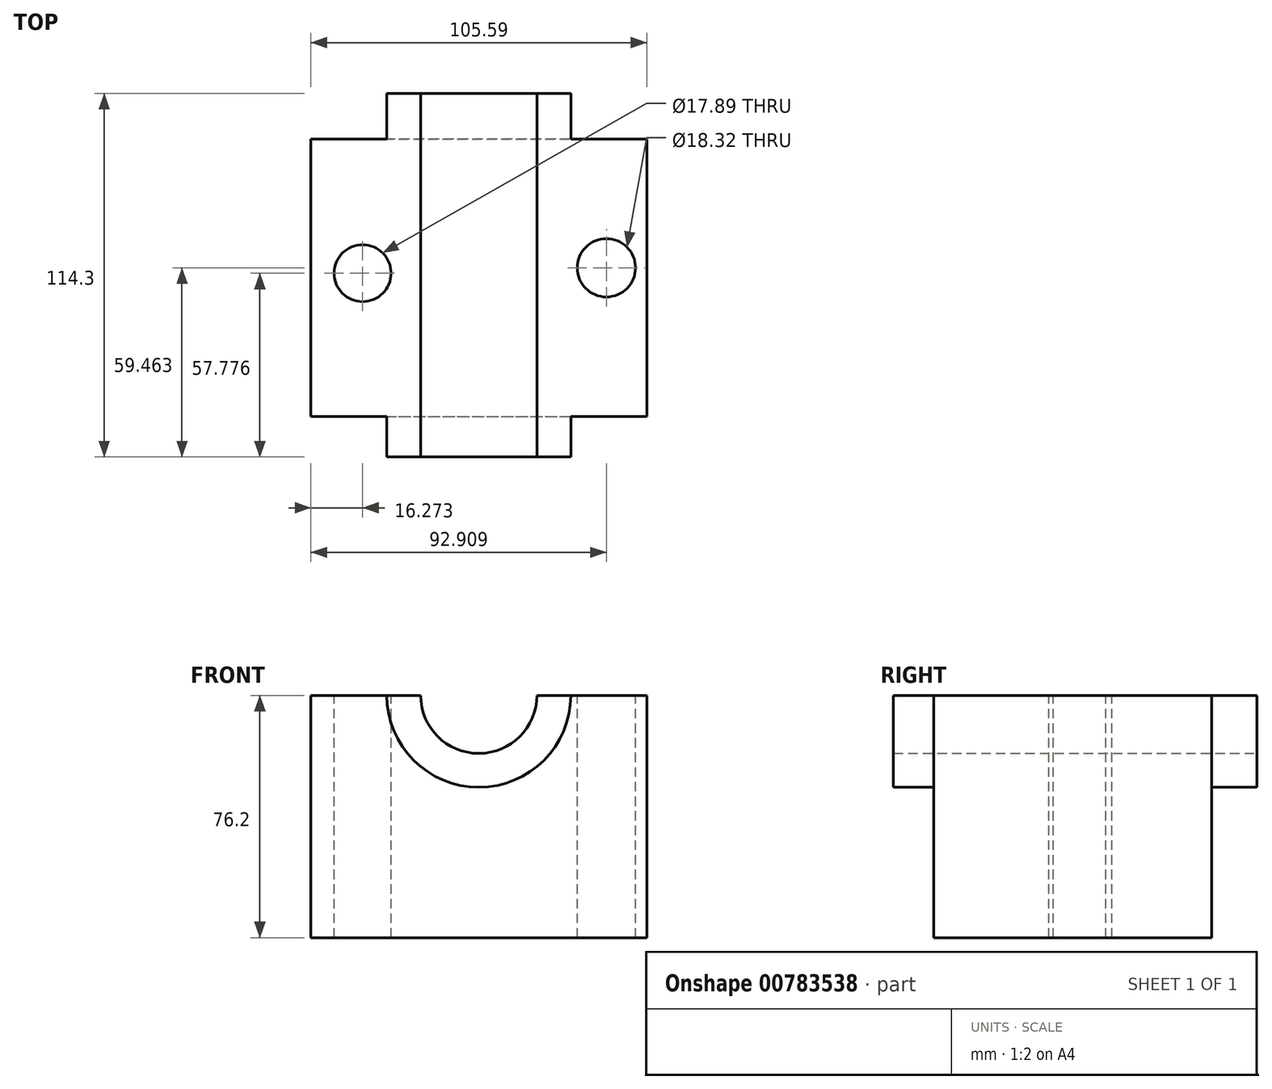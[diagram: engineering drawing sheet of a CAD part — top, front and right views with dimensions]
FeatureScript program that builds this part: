
annotation { "Feature Type Name" : "Feature", "Feature Type Description" : "" }
export const myFeature = defineFeature(function(context is Context, id is Id, definition is map)
    precondition{}
    {
        {
            var Q0;
            Q0=qCreatedBy(makeId("Top.planeOp"),FACE);
            var sketch = newSketch(context, id + "F0", { "sketchPlane" : qUnion([Q0])});
            skLineSegment(sketch, "E0.bottom", {"start": v(-49.41, 48.63) * mm, "end": v(56.18, 48.63) * mm});
            skLineSegment(sketch, "E0.top", {"start": v(-49.41, -38.7) * mm, "end": v(56.18, -38.7) * mm});
            skLineSegment(sketch, "E0.left", {"start": v(-49.41, 48.63) * mm, "end": v(-49.41, -38.7) * mm});
            skLineSegment(sketch, "E0.right", {"start": v(56.18, 48.63) * mm, "end": v(56.18, -38.7) * mm});
            skSolve(sketch);
        }
        {
            var Q0;
            Q0=makeQuery(id+"F0.imprint","IMPRINT",FACE,{"disambiguationData":[TD([[makeQuery(id+"F0.imprint","IMPRINT",EDGE,{"derivedFrom":sQuery(id+"F0.wireOp",EDGE,"E0.bottom")}),-1.0]])]});
            extrude(context, id + "F1", {"entities" : qUnion([Q0]), "depth" : 76.2 * mm, "offsetDistance" : 25.4 * mm});
        }
        {
            var Q0;
            Q0=makeQuery(id+"F1.opExtrude","SWEPT_FACE",FACE,{"disambiguationData":[OSD([sQuery(id+"F0.wireOp",EDGE,"E0.top")])]});
            var sketch = newSketch(context, id + "F2", { "sketchPlane" : qUnion([Q0])});
            skCircle(sketch, "E1", {"center": v(3.38, 76.2) * mm, "radius": 28.92 * mm});
            skCircle(sketch, "E2", {"center": v(3.38, 76.2) * mm, "radius": 18.26 * mm});
            skSolve(sketch);
        }
        {
            var Q0;
            {var subQ0=sQuery(id+"F2.wireOp",EDGE,"E2");var subQ1=makeQuery(id+"F1.opExtrude","CAP_EDGE",EDGE,{"disambiguationData":[OSD([sQuery(id+"F0.wireOp",EDGE,"E0.top")])],"isStart":false});var subQ2=makeQuery(id+"F2.imprint","INTERSECT",VERTEX,{"disambiguationData":[OD(0.0)],"derivedFrom":[subQ1,subQ0]});Q0=makeQuery(id+"F2.imprint","IMPRINT",FACE,{"disambiguationData":[TD([[makeQuery(id+"F2.imprint","IMPRINT",EDGE,{"disambiguationData":[TD([[subQ2,-1.0]])],"derivedFrom":subQ0}),1.0]])]});}
            var Q1;
            {var subQ0=sQuery(id+"F2.wireOp",EDGE,"E1");var subQ1=makeQuery(id+"F1.opExtrude","CAP_EDGE",EDGE,{"disambiguationData":[OSD([sQuery(id+"F0.wireOp",EDGE,"E0.top")])],"isStart":false});var subQ2=makeQuery(id+"F2.imprint","INTERSECT",VERTEX,{"disambiguationData":[OD(0.0)],"derivedFrom":[subQ1,subQ0]});Q1=makeQuery(id+"F2.imprint","IMPRINT",FACE,{"disambiguationData":[TD([[makeQuery(id+"F2.imprint","IMPRINT",EDGE,{"disambiguationData":[TD([[subQ2,-1.0]])],"derivedFrom":subQ0}),1.0]])]});}
            extrude(context, id + "F3", {"entities" : qUnion([Q0, Q1]), "operationType" : NewBodyOperationType.ADD, "oppositeDirection" : true, "depth" : 101.6 * mm, "offsetDistance" : 25.4 * mm});
        }
        {
            var Q0;
            {var subQ0=sQuery(id+"F2.wireOp",EDGE,"E1");var subQ1=makeQuery(id+"F1.opExtrude","CAP_EDGE",EDGE,{"disambiguationData":[OSD([sQuery(id+"F0.wireOp",EDGE,"E0.top")])],"isStart":false});var subQ2=makeQuery(id+"F2.imprint","INTERSECT",VERTEX,{"disambiguationData":[OD(0.0)],"derivedFrom":[subQ1,subQ0]});Q0=makeQuery(id+"F2.imprint","IMPRINT",FACE,{"disambiguationData":[TD([[makeQuery(id+"F2.imprint","IMPRINT",EDGE,{"disambiguationData":[TD([[subQ2,-1.0]])],"derivedFrom":subQ0}),1.0]])]});}
            extrude(context, id + "F4", {"entities" : qUnion([Q0]), "operationType" : NewBodyOperationType.ADD, "depth" : 12.7 * mm, "offsetDistance" : 25.4 * mm});
        }
        {
            var Q0;
            {var subQ1=sQuery(id+"F0.wireOp",EDGE,"E0.top");var subQ3=sQuery(id+"F2.wireOp",EDGE,"E2");Q0=makeQuery(id+"F4.boolean.opBoolean","SPLIT",FACE,{"disambiguationData":[TD([makeQuery(id+"F4.opExtrude","SWEPT_FACE",FACE,{"disambiguationData":[OSD([subQ3])]})])],"derivedFrom":makeQuery(id+"F1.opExtrude","SWEPT_FACE",FACE,{"disambiguationData":[OSD([subQ1])]})});}
            extrude(context, id + "F5", {"entities" : qUnion([Q0]), "operationType" : NewBodyOperationType.REMOVE, "oppositeDirection" : true, "depth" : 127 * mm, "offsetDistance" : 25.4 * mm});
        }
        {
            var Q0;
            {var subQ0=sQuery(id+"F2.wireOp",EDGE,"E1");var subQ2=sQuery(id+"F0.wireOp",EDGE,"E0.top");var subQ3=sQuery(id+"F0.wireOp",EDGE,"E0.right");var subQ4=sQuery(id+"F0.wireOp",EDGE,"E0.bottom");var subQ5=makeQuery(id+"F1.opExtrude","CAP_EDGE",EDGE,{"disambiguationData":[OSD([subQ2])],"isStart":false});Q0=makeQuery(id+"F5.boolean.opBoolean","SPLIT",FACE,{"disambiguationData":[TD([makeQuery(id+"F1.opExtrude","SWEPT_FACE",FACE,{"disambiguationData":[OSD([subQ3])]})])],"derivedFrom":makeQuery(id+"F4.boolean.opBoolean","MERGE",FACE,{"derivedFrom":[makeQuery(id+"F3.boolean.opBoolean","MERGE",FACE,{"derivedFrom":[makeQuery(id+"F1.opExtrude","CAP_FACE",FACE,{"disambiguationData":[OSD([subQ4,subQ2,sQuery(id+"F0.wireOp",EDGE,"E0.left"),subQ3])],"isStart":false}),makeQuery(id+"F3.opExtrude","SWEPT_FACE",FACE,{"disambiguationData":[OSD([subQ2])]})]}),makeQuery(id+"F4.opExtrude","SWEPT_FACE",FACE,{"disambiguationData":[OSD([subQ2]),TDD([makeQuery(id+"F2.imprint","IMPRINT",EDGE,{"disambiguationData":[TD([[makeQuery(id+"F2.imprint","INTERSECT",VERTEX,{"disambiguationData":[OD(0.0)],"derivedFrom":[subQ5,subQ0]}),-1.0]])],"derivedFrom":subQ5})])]}),makeQuery(id+"F4.opExtrude","SWEPT_FACE",FACE,{"disambiguationData":[OSD([subQ2]),TDD([makeQuery(id+"F2.imprint","IMPRINT",EDGE,{"disambiguationData":[TD([[makeQuery(id+"F2.imprint","INTERSECT",VERTEX,{"disambiguationData":[OD(1.0)],"derivedFrom":[subQ5,subQ0]}),1.0]])],"derivedFrom":subQ5})])]})]})});}
            var sketch = newSketch(context, id + "F6", { "sketchPlane" : qUnion([Q0])});
            skCircle(sketch, "E3", {"center": v(43.5, 8.07) * mm, "radius": 9.16 * mm});
            skCircle(sketch, "E4", {"center": v(-33.14, 6.39) * mm, "radius": 8.95 * mm});
            skSolve(sketch);
        }
        {
            var Q0;
            Q0=makeQuery(id+"F6.imprint","IMPRINT",FACE,{"disambiguationData":[TD([[makeQuery(id+"F6.imprint","IMPRINT",EDGE,{"derivedFrom":sQuery(id+"F6.wireOp",EDGE,"E4")}),1.0]])]});
            extrude(context, id + "F7", {"entities" : qUnion([Q0]), "operationType" : NewBodyOperationType.REMOVE, "oppositeDirection" : true, "depth" : 101.6 * mm, "offsetDistance" : 25.4 * mm});
        }
        {
            var Q0;
            Q0=makeQuery(id+"F6.imprint","IMPRINT",FACE,{"disambiguationData":[TD([[makeQuery(id+"F6.imprint","IMPRINT",EDGE,{"derivedFrom":sQuery(id+"F6.wireOp",EDGE,"E3")}),1.0]])]});
            extrude(context, id + "F8", {"entities" : qUnion([Q0]), "operationType" : NewBodyOperationType.REMOVE, "oppositeDirection" : true, "depth" : 127 * mm, "offsetDistance" : 25.4 * mm});
        }
    });
